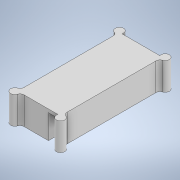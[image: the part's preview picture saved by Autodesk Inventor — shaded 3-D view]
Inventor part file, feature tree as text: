
AUTODESK INVENTOR PART (.ipt)
format: ipt  version: 2020 (Build 240168000, 168)  size: 215,040 bytes
history: native  units: in
note: dims shown in document units (in); Inventor stores cm internally (conversion verified against a paired STEP export)
features: extrude x7, sketch x7, projected_geometry x4, fillet x3, mirror x3, plane x2
ambient origin geometry x8: Origin, YZ Plane, XZ Plane, XY Plane, X Axis, Y Axis, Z Axis, Center Point
bodies: Solid1 (feature_tree)
feature tree (26):
  extrude  "Extrusion1"  Depth=2.5in
  extrude  "Extrusion2"  Depth=0.75in TaperAngle=0.0deg
  extrude  "Extrusion3"  Depth=0.1in
  extrude  "Extrusion4"  Depth=0.33in
  extrude  "Extrusion5"  Depth=0.25in
  extrude  "Extrusion6"  Depth=0.1in TaperAngle=0.0deg
  extrude  "Extrusion7"  Depth=0.125in
  fillet  "Fillet1"  Radius=0.08in
  plane  "Work Plane1"
  mirror  "Mirror1"
  plane  "Work Plane2"
  mirror  "Mirror2"
  fillet  "Fillet2"  Radius=0.13in
  mirror  "Mirror3"
  fillet  "Fillet3"  Radius=0.4in
  sketch  "Sketch1"  dims[d0=1.08in d1=2.5in]
  sketch  "Sketch2"  dims[d2=0.125in d3=0.75in d4=0.0in]
  projected_geometry  "Projected Loop1"
  sketch  "Sketch3"  dims[d5=0.1in d6=0.0in d7=0.1in]
  sketch  "Sketch4"  dims[d8=0.63in d9=0.33in]
  sketch  "Sketch5"  dims[d10=0.1in d11=0.0in d12=0.25in]
  projected_geometry  "Projected Loop2"
  sketch  "Sketch6"  dims[d13=0.1in d14=0.0in d15=0.4in d16=0.0in]
  projected_geometry  "Projected Loop3"
  sketch  "Sketch7"  dims[d17=0.1in d18=0.08in d19=0.08in d20=0.13in d21=0.4in d22=0.0in d23=0.4in d24=0.0in d25=0.125in d26=0.125in d27=0.125in]
  projected_geometry  "Projected Loop4"
